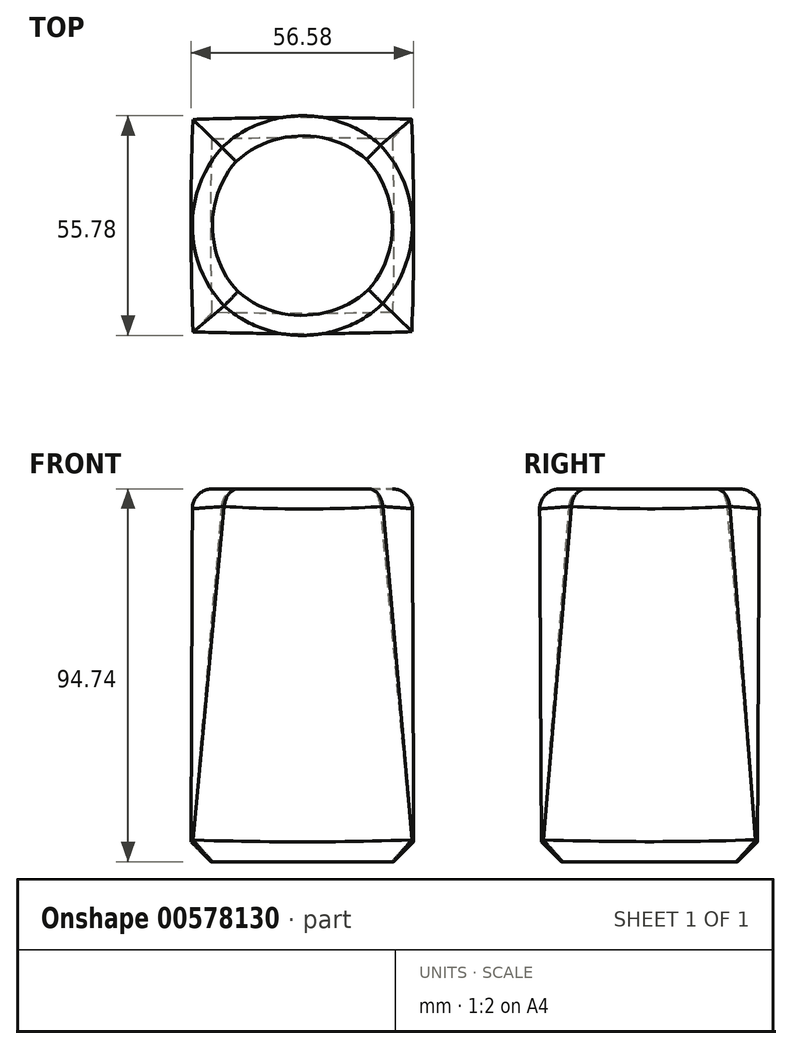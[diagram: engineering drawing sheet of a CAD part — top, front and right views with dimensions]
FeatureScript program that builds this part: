
annotation { "Feature Type Name" : "Feature", "Feature Type Description" : "" }
export const myFeature = defineFeature(function(context is Context, id is Id, definition is map)
    precondition{}
    {
        {
            var Q0;
            Q0=qCreatedBy(makeId("Top.planeOp"),FACE);
            cPlane(context, id + "F0", {"entities" : qUnion([Q0]), "cplaneType" : CPlaneType.OFFSET, "offset" : 94.74 * mm, "width" : 152.4 * mm, "height" : 152.4 * mm});
        }
        {
            var Q0;
            Q0=qCreatedBy(makeId("Top.planeOp"),FACE);
            var sketch = newSketch(context, id + "F1", { "sketchPlane" : qUnion([Q0])});
            skLineSegment(sketch, "E0.bottom", {"start": v(28.3, -27.42) * mm, "end": v(-28.3, -27.42) * mm});
            skLineSegment(sketch, "E0.top", {"start": v(28.3, 27.42) * mm, "end": v(-28.3, 27.42) * mm});
            skLineSegment(sketch, "E0.left", {"start": v(28.3, -27.42) * mm, "end": v(28.3, 27.42) * mm});
            skLineSegment(sketch, "E0.right", {"start": v(-28.3, -27.42) * mm, "end": v(-28.3, 27.42) * mm});
            skPoint(sketch, "E0.middle", {"position": v(0, 0) * mm});
            skSolve(sketch);
        }
        {
            var Q0;
            Q0=qCreatedBy(id+"F0.planeOp",FACE);
            var sketch = newSketch(context, id + "F2", { "sketchPlane" : qUnion([Q0])});
            skCircle(sketch, "E1", {"center": v(0, 0) * mm, "radius": 27.92 * mm});
            skSolve(sketch);
        }
        {
            var Q0;
            Q0=makeQuery(id+"F1.imprint","IMPRINT",FACE,{"disambiguationData":[TD([[makeQuery(id+"F1.imprint","IMPRINT",EDGE,{"derivedFrom":sQuery(id+"F1.wireOp",EDGE,"E0.bottom")}),-1.0]])]});
            var Q1;
            Q1=makeQuery(id+"F2.imprint","IMPRINT",FACE,{"disambiguationData":[TD([[makeQuery(id+"F2.imprint","IMPRINT",EDGE,{"derivedFrom":sQuery(id+"F2.wireOp",EDGE,"E1")}),1.0]])]});
            loft(context, id + "F3", {"sheetProfilesArray" : [{ "sheetProfileEntities" : qUnion([Q0]) }, { "sheetProfileEntities" : qUnion([Q1]) }]});
        }
        {
            var Q0;
            Q0=makeQuery(id+"F3.opLoft","CAP_FACE",FACE,{"disambiguationData":[OSD([makeQuery(id+"F2.imprint","IMPRINT",FACE,{"disambiguationData":[TD([[makeQuery(id+"F2.imprint","IMPRINT",EDGE,{"derivedFrom":sQuery(id+"F2.wireOp",EDGE,"E1")}),1.0]])]})])],"isStart":true});
            fillet(context, id + "F4", {"entities" : qUnion([Q0]), "radius" : 5.08 * mm, "tangentPropagation" : true, "allowEdgeOverflow" : false});
        }
        {
            var Q0;
            Q0=makeQuery(id+"F3.opLoft","CAP_FACE",FACE,{"disambiguationData":[OSD([makeQuery(id+"F1.imprint","IMPRINT",FACE,{"disambiguationData":[TD([[makeQuery(id+"F1.imprint","IMPRINT",EDGE,{"derivedFrom":sQuery(id+"F1.wireOp",EDGE,"E0.bottom")}),-1.0]])]})])],"isStart":true});
            chamfer(context, id + "F5", {"entities" : qUnion([Q0]), "width" : 5.08 * mm, "tangentPropagation" : true});
        }
    });
